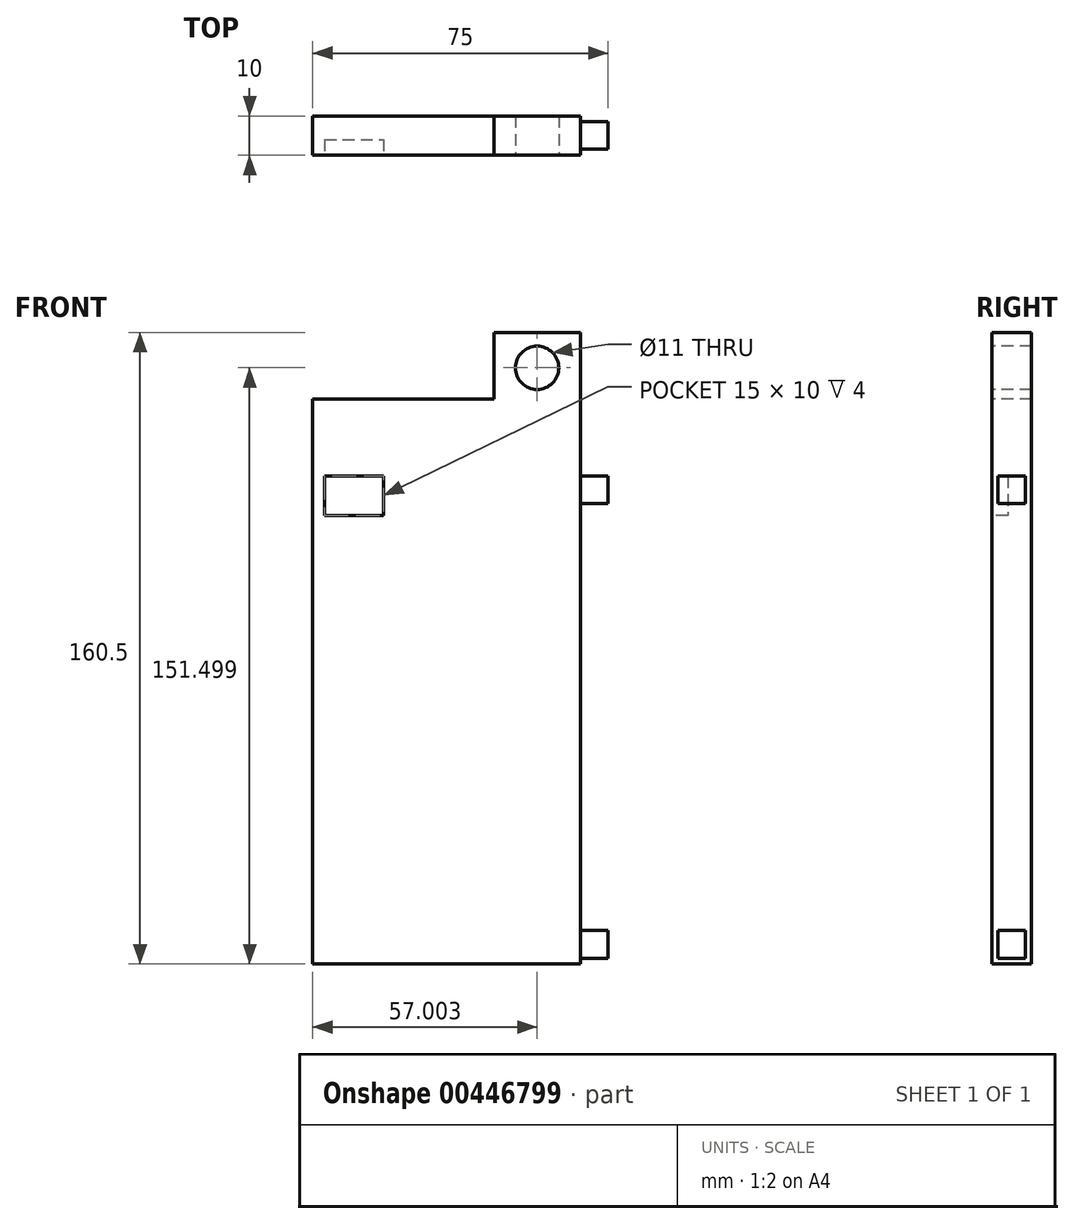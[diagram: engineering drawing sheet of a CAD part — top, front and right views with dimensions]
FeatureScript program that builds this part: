
annotation { "Feature Type Name" : "Feature", "Feature Type Description" : "" }
export const myFeature = defineFeature(function(context is Context, id is Id, definition is map)
    precondition{}
    {
        {
            var Q0;
            Q0=qCreatedBy(makeId("Front.planeOp"),FACE);
            var sketch = newSketch(context, id + "F0", { "sketchPlane" : qUnion([Q0])});
            skLineSegment(sketch, "E0.bottom", {"start": v(-29.83, 107.13) * mm, "end": v(38.17, 107.13) * mm});
            skLineSegment(sketch, "E0.top", {"start": v(-29.83, -53.37) * mm, "end": v(38.17, -53.37) * mm});
            skLineSegment(sketch, "E0.left", {"start": v(-29.83, 107.13) * mm, "end": v(-29.83, -53.37) * mm});
            skLineSegment(sketch, "E0.right", {"start": v(38.17, 107.13) * mm, "end": v(38.17, -53.37) * mm});
            skSolve(sketch);
        }
        {
            var Q0;
            Q0=makeQuery(id+"F0.imprint","IMPRINT",FACE,{"disambiguationData":[TD([[makeQuery(id+"F0.imprint","IMPRINT",EDGE,{"derivedFrom":sQuery(id+"F0.wireOp",EDGE,"E0.bottom")}),-1.0]])]});
            extrude(context, id + "F1", {"entities" : qUnion([Q0]), "depth" : 10 * mm});
        }
        {
            var Q0;
            Q0=makeQuery(id+"F1.opExtrude","CAP_FACE",FACE,{"disambiguationData":[OSD([sQuery(id+"F0.wireOp",EDGE,"E0.bottom"),sQuery(id+"F0.wireOp",EDGE,"E0.top"),sQuery(id+"F0.wireOp",EDGE,"E0.left"),sQuery(id+"F0.wireOp",EDGE,"E0.right")])],"isStart":false});
            var sketch = newSketch(context, id + "F2", { "sketchPlane" : qUnion([Q0])});
            skLineSegment(sketch, "E1.bottom", {"start": v(-29.83, 107.13) * mm, "end": v(16.17, 107.13) * mm});
            skLineSegment(sketch, "E1.top", {"start": v(-29.83, 90.13) * mm, "end": v(16.17, 90.13) * mm});
            skLineSegment(sketch, "E1.left", {"start": v(-29.83, 107.13) * mm, "end": v(-29.83, 90.13) * mm});
            skLineSegment(sketch, "E1.right", {"start": v(16.17, 107.13) * mm, "end": v(16.17, 90.13) * mm});
            skSolve(sketch);
        }
        {
            var Q0;
            Q0=qSketchRegion(id+"F2",true);
            extrude(context, id + "F3", {"entities" : qUnion([Q0]), "operationType" : NewBodyOperationType.REMOVE, "oppositeDirection" : true, "depth" : 25 * mm});
        }
        {
            var Q0;
            Q0=makeQuery(id+"F1.opExtrude","CAP_FACE",FACE,{"disambiguationData":[OSD([sQuery(id+"F0.wireOp",EDGE,"E0.bottom"),sQuery(id+"F0.wireOp",EDGE,"E0.top"),sQuery(id+"F0.wireOp",EDGE,"E0.left"),sQuery(id+"F0.wireOp",EDGE,"E0.right")])],"isStart":false});
            var sketch = newSketch(context, id + "F4", { "sketchPlane" : qUnion([Q0])});
            skCircle(sketch, "E2", {"center": v(27.17, 98.13) * mm, "radius": 5.5 * mm});
            skSolve(sketch);
        }
        {
            var Q0;
            Q0=makeQuery(id+"F4.imprint","IMPRINT",FACE,{"disambiguationData":[TD([[makeQuery(id+"F4.imprint","IMPRINT",EDGE,{"derivedFrom":sQuery(id+"F4.wireOp",EDGE,"E2")}),1.0]])]});
            extrude(context, id + "F5", {"entities" : qUnion([Q0]), "operationType" : NewBodyOperationType.REMOVE, "oppositeDirection" : true, "depth" : 25 * mm});
        }
        {
            var Q0;
            Q0=makeQuery(id+"F1.opExtrude","CAP_FACE",FACE,{"disambiguationData":[OSD([sQuery(id+"F0.wireOp",EDGE,"E0.bottom"),sQuery(id+"F0.wireOp",EDGE,"E0.top"),sQuery(id+"F0.wireOp",EDGE,"E0.left"),sQuery(id+"F0.wireOp",EDGE,"E0.right")])],"isStart":false});
            var sketch = newSketch(context, id + "F6", { "sketchPlane" : qUnion([Q0])});
            skLineSegment(sketch, "E3.0.0", {"start": v(38.17, 107.13) * mm, "end": v(16.17, 107.13) * mm});
            skLineSegment(sketch, "E3.0.1", {"start": v(16.17, 107.13) * mm, "end": v(16.17, 90.13) * mm});
            skLineSegment(sketch, "E3.0.2", {"start": v(16.17, 90.13) * mm, "end": v(-29.83, 90.13) * mm});
            skLineSegment(sketch, "E3.0.3", {"start": v(-29.83, 90.13) * mm, "end": v(-29.83, -53.37) * mm});
            skLineSegment(sketch, "E3.0.4", {"start": v(-29.83, -53.37) * mm, "end": v(38.17, -53.37) * mm});
            skLineSegment(sketch, "E3.0.5", {"start": v(38.17, -53.37) * mm, "end": v(38.17, 107.13) * mm});
            skLineSegment(sketch, "E4.bottom", {"start": v(-26.83, 70.63) * mm, "end": v(-11.83, 70.63) * mm});
            skLineSegment(sketch, "E4.top", {"start": v(-26.83, 60.63) * mm, "end": v(-11.83, 60.63) * mm});
            skLineSegment(sketch, "E4.left", {"start": v(-26.83, 70.63) * mm, "end": v(-26.83, 60.63) * mm});
            skLineSegment(sketch, "E4.right", {"start": v(-11.83, 70.63) * mm, "end": v(-11.83, 60.63) * mm});
            skSolve(sketch);
        }
        {
            var Q0;
            Q0=makeQuery(id+"F6.imprint","IMPRINT",FACE,{"disambiguationData":[TD([[makeQuery(id+"F6.imprint","IMPRINT",EDGE,{"derivedFrom":sQuery(id+"F6.wireOp",EDGE,"E4.bottom")}),-1.0]])]});
            extrude(context, id + "F7", {"entities" : qUnion([Q0]), "operationType" : NewBodyOperationType.REMOVE, "oppositeDirection" : true, "depth" : 4 * mm});
        }
        {
            var Q0;
            Q0=makeQuery(id+"F1.opExtrude","SWEPT_FACE",FACE,{"disambiguationData":[OSD([sQuery(id+"F0.wireOp",EDGE,"E0.right")])]});
            var sketch = newSketch(context, id + "F8", { "sketchPlane" : qUnion([Q0])});
            skLineSegment(sketch, "E5.bottom", {"start": v(-8.5, -44.87) * mm, "end": v(-1.5, -44.87) * mm});
            skLineSegment(sketch, "E5.top", {"start": v(-8.5, -51.87) * mm, "end": v(-1.5, -51.87) * mm});
            skLineSegment(sketch, "E5.left", {"start": v(-8.5, -44.87) * mm, "end": v(-8.5, -51.87) * mm});
            skLineSegment(sketch, "E5.right", {"start": v(-1.5, -44.87) * mm, "end": v(-1.5, -51.87) * mm});
            skLineSegment(sketch, "E6.bottom", {"start": v(-8.5, 70.63) * mm, "end": v(-1.5, 70.63) * mm});
            skLineSegment(sketch, "E6.top", {"start": v(-8.5, 63.63) * mm, "end": v(-1.5, 63.63) * mm});
            skLineSegment(sketch, "E6.left", {"start": v(-8.5, 70.63) * mm, "end": v(-8.5, 63.63) * mm});
            skLineSegment(sketch, "E6.right", {"start": v(-1.5, 70.63) * mm, "end": v(-1.5, 63.63) * mm});
            skSolve(sketch);
        }
        {
            var Q0;
            Q0=qSketchRegion(id+"F8",true);
            extrude(context, id + "F9", {"entities" : qUnion([Q0]), "operationType" : NewBodyOperationType.ADD, "depth" : 7 * mm});
        }
    });
